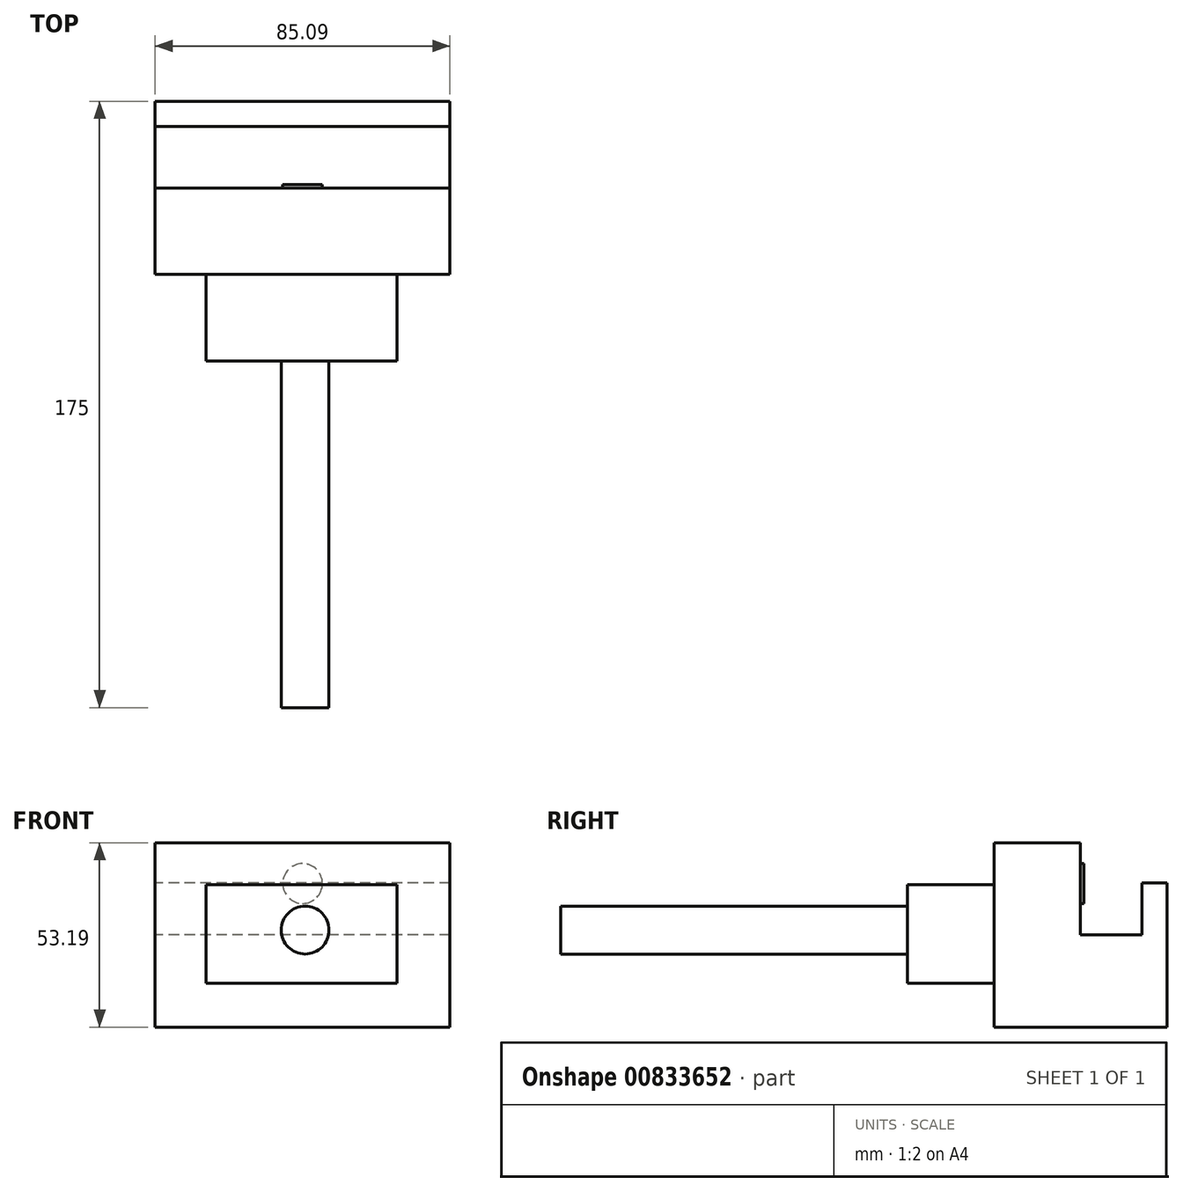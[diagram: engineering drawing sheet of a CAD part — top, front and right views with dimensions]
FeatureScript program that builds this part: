
annotation { "Feature Type Name" : "Feature", "Feature Type Description" : "" }
export const myFeature = defineFeature(function(context is Context, id is Id, definition is map)
    precondition{}
    {
        {
            var Q0;
            Q0=qCreatedBy(makeId("Front.planeOp"),FACE);
            var sketch = newSketch(context, id + "F0", { "sketchPlane" : qUnion([Q0])});
            skLineSegment(sketch, "E0.bottom", {"start": v(-45.72, 36.3) * mm, "end": v(39.37, 36.3) * mm});
            skLineSegment(sketch, "E0.top", {"start": v(-45.72, -16.89) * mm, "end": v(39.37, -16.89) * mm});
            skLineSegment(sketch, "E0.left", {"start": v(-45.72, 36.3) * mm, "end": v(-45.72, -16.89) * mm});
            skLineSegment(sketch, "E0.right", {"start": v(39.37, 36.3) * mm, "end": v(39.37, -16.89) * mm});
            skSolve(sketch);
        }
        {
            var Q0;
            Q0 = qSketchRegion(id + "F0", true);
            extrude(context, id + "F1", {"entities" : qUnion([Q0]), "depth" : 25 * mm, "offsetDistance" : 25 * mm});
        }
        {
            var Q0;
            Q0=makeQuery(id+"F1.opExtrude","CAP_FACE",FACE,{"disambiguationData":[OSD([sQuery(id+"F0.wireOp",EDGE,"E0.bottom"),sQuery(id+"F0.wireOp",EDGE,"E0.top"),sQuery(id+"F0.wireOp",EDGE,"E0.left"),sQuery(id+"F0.wireOp",EDGE,"E0.right")])],"isStart":false});
            var sketch = newSketch(context, id + "F2", { "sketchPlane" : qUnion([Q0])});
            skLineSegment(sketch, "E1.bottom", {"start": v(-30.98, 24.17) * mm, "end": v(24.07, 24.17) * mm});
            skLineSegment(sketch, "E1.top", {"start": v(-30.98, -4.2) * mm, "end": v(24.07, -4.2) * mm});
            skLineSegment(sketch, "E1.left", {"start": v(-30.98, 24.17) * mm, "end": v(-30.98, -4.2) * mm});
            skLineSegment(sketch, "E1.right", {"start": v(24.07, 24.17) * mm, "end": v(24.07, -4.2) * mm});
            skSolve(sketch);
        }
        {
            var Q0;
            Q0=makeQuery(id+"F2.imprint","IMPRINT",FACE,{"disambiguationData":[TD([[makeQuery(id+"F2.imprint","IMPRINT",EDGE,{"derivedFrom":sQuery(id+"F2.wireOp",EDGE,"E1.bottom")}),-1.0]])]});
            extrude(context, id + "F3", {"entities" : qUnion([Q0]), "operationType" : NewBodyOperationType.ADD, "depth" : 25 * mm, "offsetDistance" : 25 * mm});
        }
        {
            var Q0;
            Q0=makeQuery(id+"F3.opExtrude","CAP_FACE",FACE,{"disambiguationData":[OSD([sQuery(id+"F2.wireOp",EDGE,"E1.bottom"),sQuery(id+"F2.wireOp",EDGE,"E1.top"),sQuery(id+"F2.wireOp",EDGE,"E1.left"),sQuery(id+"F2.wireOp",EDGE,"E1.right")])],"isStart":false});
            var sketch = newSketch(context, id + "F4", { "sketchPlane" : qUnion([Q0])});
            skCircle(sketch, "E2", {"center": v(-2.43, 11.1) * mm, "radius": 6.9 * mm});
            skSolve(sketch);
        }
        {
            var Q0;
            Q0=makeQuery(id+"F4.imprint","IMPRINT",FACE,{"disambiguationData":[TD([[makeQuery(id+"F4.imprint","IMPRINT",EDGE,{"derivedFrom":sQuery(id+"F4.wireOp",EDGE,"E2")}),1.0]])]});
            extrude(context, id + "F5", {"entities" : qUnion([Q0]), "operationType" : NewBodyOperationType.ADD, "depth" : 100 * mm, "offsetDistance" : 25 * mm});
        }
        {
            var Q0;
            Q0=makeQuery(id+"F1.opExtrude","CAP_FACE",FACE,{"disambiguationData":[OSD([sQuery(id+"F0.wireOp",EDGE,"E0.bottom"),sQuery(id+"F0.wireOp",EDGE,"E0.top"),sQuery(id+"F0.wireOp",EDGE,"E0.left"),sQuery(id+"F0.wireOp",EDGE,"E0.right")])],"isStart":true});
            var sketch = newSketch(context, id + "F6", { "sketchPlane" : qUnion([Q0])});
            skLineSegment(sketch, "E3.bottom", {"start": v(-39.37, 9.7) * mm, "end": v(45.72, 9.7) * mm});
            skLineSegment(sketch, "E3.top", {"start": v(-39.37, -16.89) * mm, "end": v(45.72, -16.89) * mm});
            skLineSegment(sketch, "E3.left", {"start": v(-39.37, 9.7) * mm, "end": v(-39.37, -16.89) * mm});
            skLineSegment(sketch, "E3.right", {"start": v(45.72, 9.7) * mm, "end": v(45.72, -16.89) * mm});
            skSolve(sketch);
        }
        {
            var Q0;
            Q0=makeQuery(id+"F6.imprint","IMPRINT",FACE,{"disambiguationData":[TD([[makeQuery(id+"F6.imprint","IMPRINT",EDGE,{"derivedFrom":sQuery(id+"F6.wireOp",EDGE,"E3.bottom")}),-1.0]])]});
            extrude(context, id + "F7", {"entities" : qUnion([Q0]), "operationType" : NewBodyOperationType.ADD, "depth" : 25 * mm, "offsetDistance" : 25 * mm});
        }
        {
            var Q0;
            Q0=makeQuery(id+"F7.opExtrude","SWEPT_FACE",FACE,{"disambiguationData":[OSD([sQuery(id+"F6.wireOp",EDGE,"E3.bottom")])]});
            var sketch = newSketch(context, id + "F8", { "sketchPlane" : qUnion([Q0])});
            skLineSegment(sketch, "E4.bottom", {"start": v(-45.72, 25) * mm, "end": v(39.37, 25) * mm});
            skLineSegment(sketch, "E4.top", {"start": v(-45.72, 17.78) * mm, "end": v(39.37, 17.78) * mm});
            skLineSegment(sketch, "E4.left", {"start": v(-45.72, 25) * mm, "end": v(-45.72, 17.78) * mm});
            skLineSegment(sketch, "E4.right", {"start": v(39.37, 25) * mm, "end": v(39.37, 17.78) * mm});
            skSolve(sketch);
        }
        {
            var Q0;
            Q0=makeQuery(id+"F8.imprint","IMPRINT",FACE,{"disambiguationData":[TD([[makeQuery(id+"F8.imprint","IMPRINT",EDGE,{"derivedFrom":sQuery(id+"F8.wireOp",EDGE,"E4.bottom")}),1.0]])]});
            extrude(context, id + "F9", {"entities" : qUnion([Q0]), "operationType" : NewBodyOperationType.ADD, "depth" : 15 * mm, "offsetDistance" : 25 * mm});
        }
        {
            var Q0;
            Q0=makeQuery(id+"F1.opExtrude","CAP_FACE",FACE,{"disambiguationData":[OSD([sQuery(id+"F0.wireOp",EDGE,"E0.bottom"),sQuery(id+"F0.wireOp",EDGE,"E0.top"),sQuery(id+"F0.wireOp",EDGE,"E0.left"),sQuery(id+"F0.wireOp",EDGE,"E0.right")])],"isStart":true});
            var sketch = newSketch(context, id + "F10", { "sketchPlane" : qUnion([Q0])});
            skCircle(sketch, "E5", {"center": v(3.17, 24.54) * mm, "radius": 5.74 * mm});
            skPoint(sketch, "E5.centerSnap0", {"position": v(3.17, 36.3) * mm});
            skSolve(sketch);
        }
        {
            var Q0;
            Q0=makeQuery(id+"F10.imprint","IMPRINT",FACE,{"disambiguationData":[TD([[makeQuery(id+"F10.imprint","IMPRINT",EDGE,{"derivedFrom":sQuery(id+"F10.wireOp",EDGE,"E5")}),1.0]])]});
            extrude(context, id + "F11", {"entities" : qUnion([Q0]), "operationType" : NewBodyOperationType.ADD, "depth" : 1 * mm, "offsetDistance" : 25 * mm});
        }
    });
